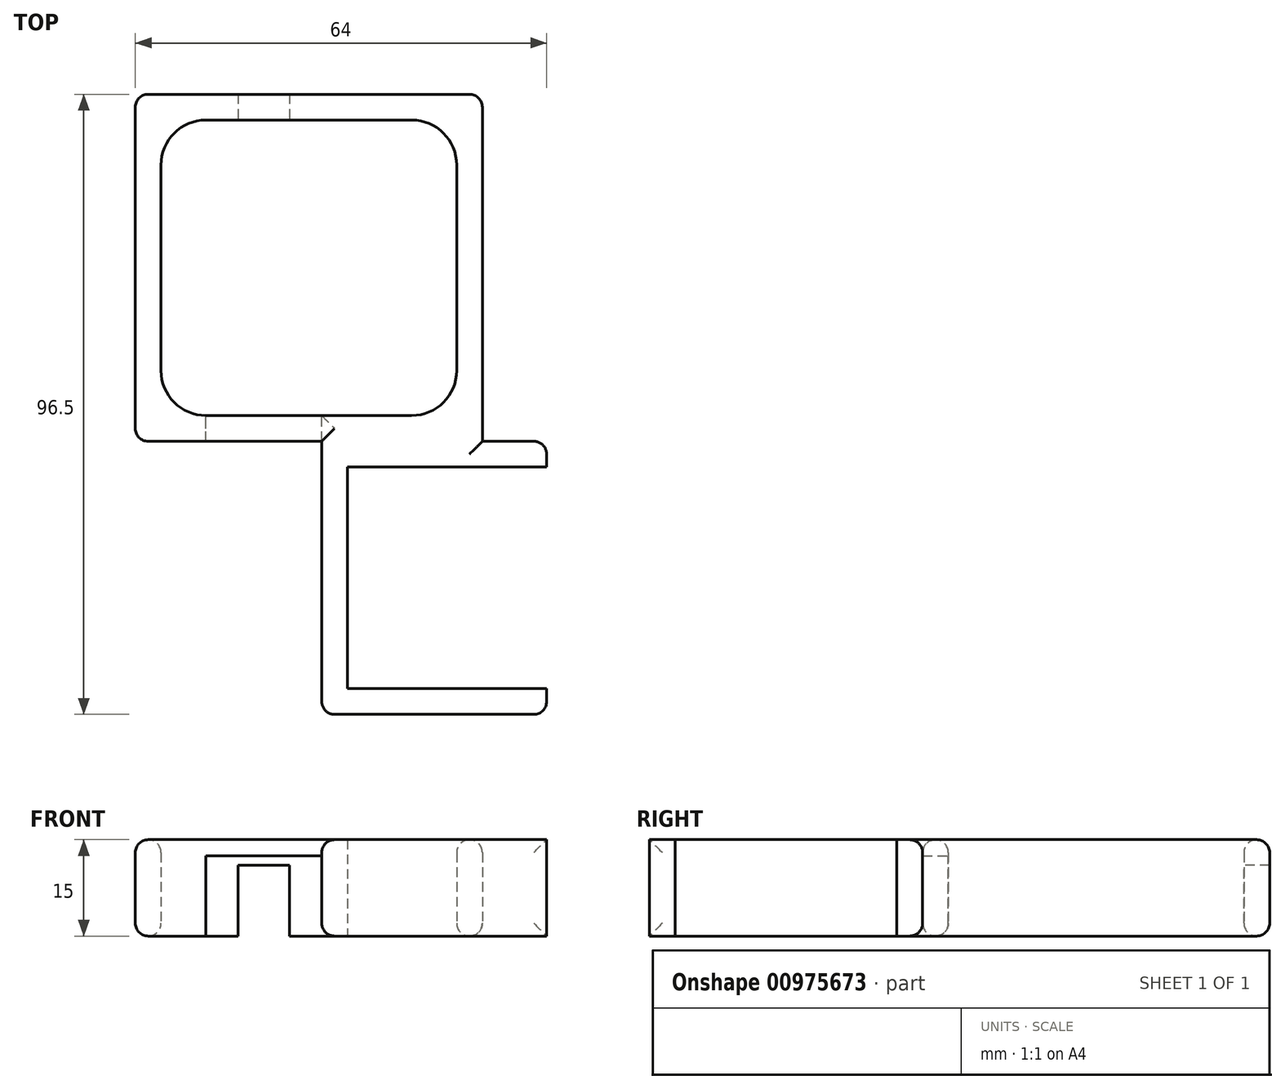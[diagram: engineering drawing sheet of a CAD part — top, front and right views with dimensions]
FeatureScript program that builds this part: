
annotation { "Feature Type Name" : "Feature", "Feature Type Description" : "" }
export const myFeature = defineFeature(function(context is Context, id is Id, definition is map)
    precondition{}
    {
        {
            var Q0;
            Q0=qCreatedBy(makeId("Top.planeOp"),FACE);
            var sketch = newSketch(context, id + "F0", { "sketchPlane" : qUnion([Q0])});
            skLineSegment(sketch, "E0", {"start": v(29.47, 14.54) * mm, "end": v(29.47, 10.54) * mm});
            skLineSegment(sketch, "E1", {"start": v(29.47, 10.54) * mm, "end": v(-1.53, 10.54) * mm});
            skLineSegment(sketch, "E2", {"start": v(-1.53, 10.54) * mm, "end": v(-1.53, -23.96) * mm});
            skLineSegment(sketch, "E3", {"start": v(-1.53, -23.96) * mm, "end": v(29.47, -23.96) * mm});
            skLineSegment(sketch, "E4", {"start": v(29.47, -23.96) * mm, "end": v(29.47, -27.96) * mm});
            skLineSegment(sketch, "E5", {"start": v(29.47, -27.96) * mm, "end": v(-5.53, -27.96) * mm});
            skLineSegment(sketch, "E6", {"start": v(-5.53, -27.96) * mm, "end": v(-5.53, 14.54) * mm});
            skLineSegment(sketch, "E7", {"start": v(-5.53, 14.54) * mm, "end": v(29.47, 14.54) * mm});
            skLineSegment(sketch, "E8.bottom", {"start": v(29.47, -23.96) * mm, "end": v(27.47, -23.96) * mm});
            skLineSegment(sketch, "E9.bottom", {"start": v(29.47, 10.54) * mm, "end": v(27.47, 10.54) * mm});
            skPoint(sketch, "E10", {"position": v(-5.53, -6.71) * mm});
            skSolve(sketch);
        }
        {
            var Q0;
            Q0=qSketchRegion(id+"F0",true);
            extrude(context, id + "F1", {"entities" : qUnion([Q0]), "endBound" : BoundingType.SYMMETRIC, "depth" : 15 * mm, "offsetDistance" : 25 * mm});
        }
        {
            var Q0;
            Q0=qCreatedBy(makeId("Top.planeOp"),FACE);
            var sketch = newSketch(context, id + "F2", { "sketchPlane" : qUnion([Q0])});
            skPoint(sketch, "E11.0", {"position": v(-5.53, 14.54) * mm});
            skPoint(sketch, "E12.0", {"position": v(29.47, 14.54) * mm});
            skLineSegment(sketch, "E13.bottom", {"start": v(-30.53, 64.54) * mm, "end": v(-18.53, 64.54) * mm});
            skLineSegment(sketch, "E13.top", {"start": v(-30.53, 18.54) * mm, "end": v(-23.53, 18.54) * mm});
            skLineSegment(sketch, "E13.left", {"start": v(-30.53, 64.54) * mm, "end": v(-30.53, 18.54) * mm});
            skLineSegment(sketch, "E13.right", {"start": v(15.47, 64.54) * mm, "end": v(15.47, 18.54) * mm});
            skLineSegment(sketch, "E14.0", {"start": v(-34.53, 68.54) * mm, "end": v(-18.53, 68.54) * mm});
            skLineSegment(sketch, "E14.1", {"start": v(-34.53, 68.54) * mm, "end": v(-34.53, 14.54) * mm});
            skLineSegment(sketch, "E14.2", {"start": v(-34.53, 14.54) * mm, "end": v(-23.53, 14.54) * mm});
            skLineSegment(sketch, "E14.3", {"start": v(19.47, 68.54) * mm, "end": v(19.47, 14.54) * mm});
            skLineSegment(sketch, "E15", {"start": v(-5.53, 14.54) * mm, "end": v(-5.53, 18.54) * mm});
            skLineSegment(sketch, "E16.MirrorCS", {"start": v(-23.53, 14.54) * mm, "end": v(-23.53, 18.54) * mm});
            skLineSegment(sketch, "E17", {"start": v(-18.53, 79.1) * mm, "end": v(-18.53, 29.22) * mm});
            skLineSegment(sketch, "E18", {"start": v(-10.53, 79.84) * mm, "end": v(-10.53, 54.16) * mm});
            skLineSegment(sketch, "E19.trimOffspring", {"start": v(-10.53, 68.54) * mm, "end": v(19.47, 68.54) * mm});
            skLineSegment(sketch, "E20.trimOffspring", {"start": v(-10.53, 64.54) * mm, "end": v(15.47, 64.54) * mm});
            skLineSegment(sketch, "E21.trimOffspring", {"start": v(-5.53, 18.54) * mm, "end": v(15.47, 18.54) * mm});
            skLineSegment(sketch, "E22.trimOffspring", {"start": v(-5.53, 14.54) * mm, "end": v(19.47, 14.54) * mm});
            skLineSegment(sketch, "E23", {"start": v(-23.53, 14.54) * mm, "end": v(-5.53, 14.54) * mm});
            skLineSegment(sketch, "E24", {"start": v(-23.53, 18.54) * mm, "end": v(-5.53, 18.54) * mm});
            skLineSegment(sketch, "E25", {"start": v(-18.53, 68.54) * mm, "end": v(-10.53, 68.54) * mm});
            skLineSegment(sketch, "E26", {"start": v(-10.53, 64.54) * mm, "end": v(-18.53, 64.54) * mm});
            skSolve(sketch);
        }
        {
            var Q0;
            {var subQ1=sQuery(id+"F2.wireOp",EDGE,"E13.bottom");Q0=makeQuery(id+"F2.imprint","IMPRINT",FACE,{"disambiguationData":[TD([[makeQuery(id+"F2.imprint","IMPRINT",EDGE,{"derivedFrom":subQ1}),1.0]])]});}
            var Q1;
            Q1=makeQuery(id+"F2.imprint","IMPRINT",FACE,{"disambiguationData":[TD([[makeQuery(id+"F2.imprint","IMPRINT",EDGE,{"derivedFrom":sQuery(id+"F2.wireOp",EDGE,"E13.right")}),1.0]])]});
            var Q2;
            Q2=makeQuery(id+"F2.imprint","IMPRINT",FACE,{"disambiguationData":[TD([[makeQuery(id+"F2.imprint","IMPRINT",EDGE,{"derivedFrom":sQuery(id+"F2.wireOp",EDGE,"E15")}),1.0]])]});
            var Q3;
            {var subQ2=sQuery(id+"F2.wireOp",EDGE,"E25");Q3=makeQuery(id+"F2.imprint","IMPRINT",FACE,{"disambiguationData":[TD([[makeQuery(id+"F2.imprint","IMPRINT",EDGE,{"derivedFrom":subQ2}),-1.0]])]});}
            extrude(context, id + "F3", {"entities" : qUnion([Q0, Q1, Q2, Q3]), "operationType" : NewBodyOperationType.ADD, "endBound" : BoundingType.SYMMETRIC, "depth" : 15 * mm, "offsetDistance" : 25 * mm});
        }
        {
            var Q0;
            Q0=makeQuery(id+"F2.imprint","IMPRINT",FACE,{"disambiguationData":[TD([[makeQuery(id+"F2.imprint","IMPRINT",EDGE,{"derivedFrom":sQuery(id+"F2.wireOp",EDGE,"E15")}),1.0]])]});
            extrude(context, id + "F4", {"entities" : qUnion([Q0]), "operationType" : NewBodyOperationType.REMOVE, "endBound" : BoundingType.SYMMETRIC, "oppositeDirection" : true, "depth" : 10 * mm, "offsetDistance" : 25 * mm});
        }
        {
            var Q0;
            Q0=makeQuery(id+"F2.imprint","IMPRINT",FACE,{"disambiguationData":[TD([[makeQuery(id+"F2.imprint","IMPRINT",EDGE,{"derivedFrom":sQuery(id+"F2.wireOp",EDGE,"E15")}),1.0]])]});
            extrude(context, id + "F5", {"entities" : qUnion([Q0]), "operationType" : NewBodyOperationType.REMOVE, "oppositeDirection" : true, "depth" : 25 * mm, "offsetDistance" : 25 * mm});
        }
        {
            var Q0;
            {var subQ2=sQuery(id+"F2.wireOp",EDGE,"E25");Q0=makeQuery(id+"F2.imprint","IMPRINT",FACE,{"disambiguationData":[TD([[makeQuery(id+"F2.imprint","IMPRINT",EDGE,{"derivedFrom":subQ2}),-1.0]])]});}
            extrude(context, id + "F6", {"entities" : qUnion([Q0]), "operationType" : NewBodyOperationType.REMOVE, "endBound" : BoundingType.SYMMETRIC, "oppositeDirection" : true, "depth" : 7 * mm, "offsetDistance" : 25 * mm});
        }
        {
            var Q0;
            {var subQ2=sQuery(id+"F2.wireOp",EDGE,"E25");Q0=makeQuery(id+"F2.imprint","IMPRINT",FACE,{"disambiguationData":[TD([[makeQuery(id+"F2.imprint","IMPRINT",EDGE,{"derivedFrom":subQ2}),-1.0]])]});}
            extrude(context, id + "F7", {"entities" : qUnion([Q0]), "operationType" : NewBodyOperationType.REMOVE, "oppositeDirection" : true, "depth" : 25 * mm, "offsetDistance" : 25 * mm});
        }
        {
            var Q0;
            Q0=makeQuery(id+"F3.opExtrude","SWEPT_EDGE",EDGE,{"disambiguationData":[OSD([sQuery(id+"F2.wireOp",EDGE,"E13.bottom"),sQuery(id+"F2.wireOp",EDGE,"E13.left")])]});
            var Q1;
            Q1=makeQuery(id+"F3.opExtrude","SWEPT_EDGE",EDGE,{"disambiguationData":[OSD([sQuery(id+"F2.wireOp",EDGE,"E13.right"),sQuery(id+"F2.wireOp",EDGE,"E20.trimOffspring")])]});
            var Q2;
            Q2=makeQuery(id+"F3.opExtrude","SWEPT_EDGE",EDGE,{"disambiguationData":[OSD([sQuery(id+"F2.wireOp",EDGE,"E13.top"),sQuery(id+"F2.wireOp",EDGE,"E13.left")])]});
            var Q3;
            Q3=makeQuery(id+"F3.opExtrude","SWEPT_EDGE",EDGE,{"disambiguationData":[OSD([sQuery(id+"F2.wireOp",EDGE,"E13.right"),sQuery(id+"F2.wireOp",EDGE,"E21.trimOffspring")])]});
            fillet(context, id + "F8", {"entities" : qUnion([Q0, Q1, Q2, Q3]), "radius" : 7 * mm, "tangentPropagation" : true, "defaultsChanged" : true, "vertexSettings" : [], "allowEdgeOverflow" : false});
        }
        {
            var Q0;
            Q0=makeQuery(id+"F3.opExtrude","CAP_EDGE",EDGE,{"disambiguationData":[OSD([sQuery(id+"F2.wireOp",EDGE,"E14.3")])],"isStart":false});
            var Q1;
            Q1=makeQuery(id+"F3.opExtrude","CAP_EDGE",EDGE,{"disambiguationData":[OSD([sQuery(id+"F2.wireOp",EDGE,"E14.3")])],"isStart":true});
            var Q2;
            Q2=makeQuery(id+"F1.opExtrude","CAP_EDGE",EDGE,{"disambiguationData":[OSD([sQuery(id+"F0.wireOp",EDGE,"E7")])],"isStart":false});
            var Q3;
            Q3=makeQuery(id+"F1.opExtrude","CAP_EDGE",EDGE,{"disambiguationData":[OSD([sQuery(id+"F0.wireOp",EDGE,"E7")])],"isStart":true});
            var Q4;
            Q4=makeQuery(id+"F3.opExtrude","SWEPT_EDGE",EDGE,{"disambiguationData":[OSD([sQuery(id+"F2.wireOp",EDGE,"E14.3"),sQuery(id+"F2.wireOp",EDGE,"E19.trimOffspring")])]});
            var Q5;
            {var subQ0=sQuery(id+"F2.wireOp",EDGE,"E14.3");var subQ2=sQuery(id+"F2.wireOp",EDGE,"E25");var subQ3=sQuery(id+"F2.wireOp",EDGE,"E19.trimOffspring");var subQ4=sQuery(id+"F2.wireOp",EDGE,"E14.0");Q5=makeQuery(id+"F7.boolean.opBoolean","SPLIT",EDGE,{"disambiguationData":[TD([makeQuery(id+"F3.opExtrude","SWEPT_FACE",FACE,{"disambiguationData":[OSD([subQ0])]})])],"derivedFrom":makeQuery(id+"F3.opExtrude","CAP_EDGE",EDGE,{"disambiguationData":[OSD([subQ4,subQ3,subQ2])],"isStart":true})});}
            var Q6;
            Q6=makeQuery(id+"F3.opExtrude","CAP_EDGE",EDGE,{"disambiguationData":[OSD([sQuery(id+"F2.wireOp",EDGE,"E14.0"),sQuery(id+"F2.wireOp",EDGE,"E19.trimOffspring"),sQuery(id+"F2.wireOp",EDGE,"E25")])],"isStart":false});
            var Q7;
            Q7=makeQuery(id+"F6.boolean.opBoolean","COPY",EDGE,{"derivedFrom":makeQuery(id+"F6.opExtrude","CAP_EDGE",EDGE,{"disambiguationData":[OSD([sQuery(id+"F2.wireOp",EDGE,"E25")])],"isStart":true})});
            var Q8;
            {var subQ0=sQuery(id+"F2.wireOp",EDGE,"E25");var subQ1=sQuery(id+"F2.wireOp",EDGE,"E17");var subQ2=sQuery(id+"F2.wireOp",EDGE,"E14.0");Q8=makeQuery(id+"F7.boolean.opBoolean","MERGE",EDGE,{"derivedFrom":[makeQuery(id+"F6.boolean.opBoolean","COPY",EDGE,{"derivedFrom":makeQuery(id+"F6.opExtrude","SWEPT_EDGE",EDGE,{"disambiguationData":[OSD([subQ2,subQ1,subQ0])]})})],"fromTools":[makeQuery(id+"F7.opExtrude","SWEPT_EDGE",EDGE,{"disambiguationData":[OSD([subQ2,subQ1,subQ0])]})]});}
            var Q9;
            {var subQ0=sQuery(id+"F2.wireOp",EDGE,"E25");var subQ1=sQuery(id+"F2.wireOp",EDGE,"E19.trimOffspring");var subQ2=sQuery(id+"F2.wireOp",EDGE,"E18");Q9=makeQuery(id+"F7.boolean.opBoolean","MERGE",EDGE,{"derivedFrom":[makeQuery(id+"F6.boolean.opBoolean","COPY",EDGE,{"derivedFrom":makeQuery(id+"F6.opExtrude","SWEPT_EDGE",EDGE,{"disambiguationData":[OSD([subQ2,subQ1,subQ0])]})})],"fromTools":[makeQuery(id+"F7.opExtrude","SWEPT_EDGE",EDGE,{"disambiguationData":[OSD([subQ2,subQ1,subQ0])]})]});}
            var Q10;
            {var subQ0=sQuery(id+"F2.wireOp",EDGE,"E26");var subQ1=sQuery(id+"F2.wireOp",EDGE,"E20.trimOffspring");var subQ2=sQuery(id+"F2.wireOp",EDGE,"E18");Q10=makeQuery(id+"F7.boolean.opBoolean","MERGE",EDGE,{"derivedFrom":[makeQuery(id+"F6.boolean.opBoolean","COPY",EDGE,{"derivedFrom":makeQuery(id+"F6.opExtrude","SWEPT_EDGE",EDGE,{"disambiguationData":[OSD([subQ2,subQ1,subQ0])]})})],"fromTools":[makeQuery(id+"F7.opExtrude","SWEPT_EDGE",EDGE,{"disambiguationData":[OSD([subQ2,subQ1,subQ0])]})]});}
            var Q11;
            {var subQ0=sQuery(id+"F2.wireOp",EDGE,"E26");var subQ1=sQuery(id+"F2.wireOp",EDGE,"E17");var subQ2=sQuery(id+"F2.wireOp",EDGE,"E13.bottom");Q11=makeQuery(id+"F7.boolean.opBoolean","MERGE",EDGE,{"derivedFrom":[makeQuery(id+"F6.boolean.opBoolean","COPY",EDGE,{"derivedFrom":makeQuery(id+"F6.opExtrude","SWEPT_EDGE",EDGE,{"disambiguationData":[OSD([subQ2,subQ1,subQ0])]})})],"fromTools":[makeQuery(id+"F7.opExtrude","SWEPT_EDGE",EDGE,{"disambiguationData":[OSD([subQ2,subQ1,subQ0])]})]});}
            var Q12;
            Q12=makeQuery(id+"F3.opExtrude","SWEPT_EDGE",EDGE,{"disambiguationData":[OSD([sQuery(id+"F2.wireOp",EDGE,"E14.0"),sQuery(id+"F2.wireOp",EDGE,"E14.1")])]});
            var Q13;
            {var subQ0=sQuery(id+"F2.wireOp",EDGE,"E14.1");var subQ1=sQuery(id+"F2.wireOp",EDGE,"E25");var subQ2=sQuery(id+"F2.wireOp",EDGE,"E19.trimOffspring");var subQ3=sQuery(id+"F2.wireOp",EDGE,"E14.0");Q13=makeQuery(id+"F7.boolean.opBoolean","SPLIT",EDGE,{"disambiguationData":[TD([makeQuery(id+"F3.opExtrude","SWEPT_FACE",FACE,{"disambiguationData":[OSD([subQ0])]})])],"derivedFrom":makeQuery(id+"F3.opExtrude","CAP_EDGE",EDGE,{"disambiguationData":[OSD([subQ3,subQ2,subQ1])],"isStart":true})});}
            var Q14;
            Q14=makeQuery(id+"F3.opExtrude","CAP_EDGE",EDGE,{"disambiguationData":[OSD([sQuery(id+"F2.wireOp",EDGE,"E13.left")])],"isStart":true});
            var Q15;
            Q15=makeQuery(id+"F3.opExtrude","CAP_EDGE",EDGE,{"disambiguationData":[OSD([sQuery(id+"F2.wireOp",EDGE,"E13.right")])],"isStart":true});
            var Q16;
            Q16=makeQuery(id+"F3.opExtrude","CAP_EDGE",EDGE,{"disambiguationData":[OSD([sQuery(id+"F2.wireOp",EDGE,"E14.1")])],"isStart":true});
            var Q17;
            Q17=makeQuery(id+"F3.opExtrude","CAP_EDGE",EDGE,{"disambiguationData":[OSD([sQuery(id+"F2.wireOp",EDGE,"E14.2"),sQuery(id+"F2.wireOp",EDGE,"E22.trimOffspring"),sQuery(id+"F2.wireOp",EDGE,"E23")])],"isStart":true});
            var Q18;
            Q18=makeQuery(id+"F3.opExtrude","CAP_EDGE",EDGE,{"disambiguationData":[OSD([sQuery(id+"F2.wireOp",EDGE,"E14.1")])],"isStart":false});
            var Q19;
            Q19=makeQuery(id+"F3.opExtrude","CAP_EDGE",EDGE,{"disambiguationData":[OSD([sQuery(id+"F2.wireOp",EDGE,"E14.2"),sQuery(id+"F2.wireOp",EDGE,"E22.trimOffspring"),sQuery(id+"F2.wireOp",EDGE,"E23")])],"isStart":false});
            var Q20;
            Q20=makeQuery(id+"F3.opExtrude","CAP_EDGE",EDGE,{"disambiguationData":[OSD([sQuery(id+"F2.wireOp",EDGE,"E13.left")])],"isStart":false});
            var Q21;
            {var subQ0=sQuery(id+"F2.wireOp",EDGE,"E24");var subQ1=sQuery(id+"F2.wireOp",EDGE,"E16.MirrorCS");var subQ2=sQuery(id+"F2.wireOp",EDGE,"E13.top");Q21=makeQuery(id+"F5.boolean.opBoolean","MERGE",EDGE,{"derivedFrom":[makeQuery(id+"F4.boolean.opBoolean","COPY",EDGE,{"derivedFrom":makeQuery(id+"F4.opExtrude","SWEPT_EDGE",EDGE,{"disambiguationData":[OSD([subQ2,subQ1,subQ0])]})})],"fromTools":[makeQuery(id+"F5.opExtrude","SWEPT_EDGE",EDGE,{"disambiguationData":[OSD([subQ2,subQ1,subQ0])]})]});}
            var Q22;
            {var subQ0=sQuery(id+"F2.wireOp",EDGE,"E23");var subQ1=sQuery(id+"F2.wireOp",EDGE,"E16.MirrorCS");var subQ2=sQuery(id+"F2.wireOp",EDGE,"E14.2");Q22=makeQuery(id+"F5.boolean.opBoolean","MERGE",EDGE,{"derivedFrom":[makeQuery(id+"F4.boolean.opBoolean","COPY",EDGE,{"derivedFrom":makeQuery(id+"F4.opExtrude","SWEPT_EDGE",EDGE,{"disambiguationData":[OSD([subQ2,subQ1,subQ0])]})})],"fromTools":[makeQuery(id+"F5.opExtrude","SWEPT_EDGE",EDGE,{"disambiguationData":[OSD([subQ2,subQ1,subQ0])]})]});}
            var Q23;
            {var subQ0=sQuery(id+"F2.wireOp",EDGE,"E24");var subQ1=sQuery(id+"F2.wireOp",EDGE,"E21.trimOffspring");var subQ2=sQuery(id+"F2.wireOp",EDGE,"E15");Q23=makeQuery(id+"F5.boolean.opBoolean","MERGE",EDGE,{"derivedFrom":[makeQuery(id+"F4.boolean.opBoolean","COPY",EDGE,{"derivedFrom":makeQuery(id+"F4.opExtrude","SWEPT_EDGE",EDGE,{"disambiguationData":[OSD([subQ2,subQ1,subQ0])]})})],"fromTools":[makeQuery(id+"F5.opExtrude","SWEPT_EDGE",EDGE,{"disambiguationData":[OSD([subQ2,subQ1,subQ0])]})]});}
            var Q24;
            Q24=makeQuery(id+"F5.boolean.opBoolean","INTERSECT",EDGE,{"derivedFrom":[makeQuery(id+"F3.boolean.opBoolean","MERGE",FACE,{"derivedFrom":[makeQuery(id+"F1.opExtrude","CAP_FACE",FACE,{"disambiguationData":[OSD([sQuery(id+"F0.wireOp",EDGE,"E0"),sQuery(id+"F0.wireOp",EDGE,"E1"),sQuery(id+"F0.wireOp",EDGE,"E2"),sQuery(id+"F0.wireOp",EDGE,"E3"),sQuery(id+"F0.wireOp",EDGE,"E4"),sQuery(id+"F0.wireOp",EDGE,"E5"),sQuery(id+"F0.wireOp",EDGE,"E6"),sQuery(id+"F0.wireOp",EDGE,"E7"),sQuery(id+"F0.wireOp",EDGE,"E8.bottom"),sQuery(id+"F0.wireOp",EDGE,"E9.bottom")])],"isStart":true}),makeQuery(id+"F3.opExtrude","CAP_FACE",FACE,{"disambiguationData":[OSD([sQuery(id+"F2.wireOp",EDGE,"E13.bottom"),sQuery(id+"F2.wireOp",EDGE,"E13.top"),sQuery(id+"F2.wireOp",EDGE,"E13.left"),sQuery(id+"F2.wireOp",EDGE,"E13.right"),sQuery(id+"F2.wireOp",EDGE,"E14.0"),sQuery(id+"F2.wireOp",EDGE,"E14.1"),sQuery(id+"F2.wireOp",EDGE,"E14.2"),sQuery(id+"F2.wireOp",EDGE,"E14.3"),sQuery(id+"F2.wireOp",EDGE,"E19.trimOffspring"),sQuery(id+"F2.wireOp",EDGE,"E20.trimOffspring"),sQuery(id+"F2.wireOp",EDGE,"E21.trimOffspring"),sQuery(id+"F2.wireOp",EDGE,"E22.trimOffspring"),sQuery(id+"F2.wireOp",EDGE,"E23"),sQuery(id+"F2.wireOp",EDGE,"E24"),sQuery(id+"F2.wireOp",EDGE,"E25"),sQuery(id+"F2.wireOp",EDGE,"E26")])],"isStart":true})]}),makeQuery(id+"F5.opExtrude","SWEPT_FACE",FACE,{"disambiguationData":[OSD([sQuery(id+"F2.wireOp",EDGE,"E15")])]})]});
            var Q25;
            Q25=makeQuery(id+"F1.opExtrude","CAP_EDGE",EDGE,{"disambiguationData":[OSD([sQuery(id+"F0.wireOp",EDGE,"E6")])],"isStart":false});
            var Q26;
            Q26=makeQuery(id+"F1.opExtrude","SWEPT_EDGE",EDGE,{"disambiguationData":[OSD([sQuery(id+"F0.wireOp",EDGE,"E4"),sQuery(id+"F0.wireOp",EDGE,"E5")])]});
            var Q27;
            Q27=makeQuery(id+"F1.opExtrude","SWEPT_EDGE",EDGE,{"disambiguationData":[OSD([sQuery(id+"F0.wireOp",EDGE,"E5"),sQuery(id+"F0.wireOp",EDGE,"E6")])]});
            var Q28;
            Q28=makeQuery(id+"F3.opExtrude","SWEPT_EDGE",EDGE,{"disambiguationData":[OSD([sQuery(id+"F2.wireOp",EDGE,"E14.1"),sQuery(id+"F2.wireOp",EDGE,"E14.2")])]});
            var Q29;
            Q29=makeQuery(id+"F1.opExtrude","SWEPT_EDGE",EDGE,{"disambiguationData":[OSD([sQuery(id+"F0.wireOp",EDGE,"E0"),sQuery(id+"F0.wireOp",EDGE,"E7")])]});
            fillet(context, id + "F9", {"entities" : qUnion([Q0, Q1, Q2, Q3, Q4, Q5, Q6, Q7, Q8, Q9, Q10, Q11, Q12, Q13, Q14, Q15, Q16, Q17, Q18, Q19, Q20, Q21, Q22, Q23, Q24, Q25, Q26, Q27, Q28, Q29]), "radius" : 2 * mm, "tangentPropagation" : true, "allowEdgeOverflow" : false});
        }
    });
